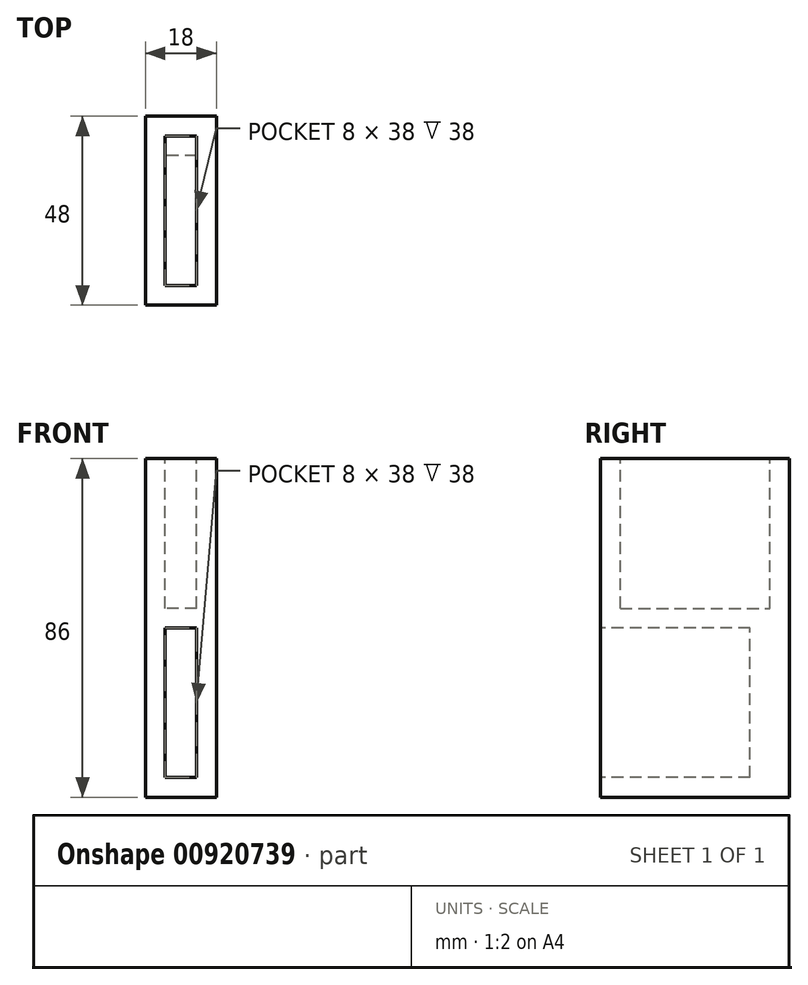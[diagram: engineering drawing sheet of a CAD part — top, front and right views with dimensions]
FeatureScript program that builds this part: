
annotation { "Feature Type Name" : "Feature", "Feature Type Description" : "" }
export const myFeature = defineFeature(function(context is Context, id is Id, definition is map)
    precondition{}
    {
        {
            var Q0;
            Q0=qCreatedBy(makeId("Top.planeOp"),FACE);
            var sketch = newSketch(context, id + "F0", { "sketchPlane" : qUnion([Q0])});
            skLineSegment(sketch, "E0.bottom", {"start": v(0, 0) * mm, "end": v(-18, 0) * mm});
            skLineSegment(sketch, "E0.top", {"start": v(0, -48) * mm, "end": v(-18, -48) * mm});
            skLineSegment(sketch, "E0.left", {"start": v(0, 0) * mm, "end": v(0, -48) * mm});
            skLineSegment(sketch, "E0.right", {"start": v(-18, 0) * mm, "end": v(-18, -48) * mm});
            skSolve(sketch);
        }
        {
            var Q0;
            Q0=makeQuery(id+"F0.imprint","IMPRINT",FACE,{"disambiguationData":[TD([[makeQuery(id+"F0.imprint","IMPRINT",EDGE,{"derivedFrom":sQuery(id+"F0.wireOp",EDGE,"E0.bottom")}),1.0]])]});
            extrude(context, id + "F1", {"entities" : qUnion([Q0]), "depth" : 86 * mm, "offsetDistance" : 25 * mm});
        }
        {
            var Q0;
            Q0=makeQuery(id+"F1.opExtrude","CAP_FACE",FACE,{"disambiguationData":[OSD([sQuery(id+"F0.wireOp",EDGE,"E0.bottom"),sQuery(id+"F0.wireOp",EDGE,"E0.top"),sQuery(id+"F0.wireOp",EDGE,"E0.left"),sQuery(id+"F0.wireOp",EDGE,"E0.right")])],"isStart":false});
            var sketch = newSketch(context, id + "F2", { "sketchPlane" : qUnion([Q0])});
            skLineSegment(sketch, "E1.bottom", {"start": v(-5, -43) * mm, "end": v(-13, -43) * mm});
            skLineSegment(sketch, "E1.top", {"start": v(-5, -5) * mm, "end": v(-13, -5) * mm});
            skLineSegment(sketch, "E1.left", {"start": v(-5, -43) * mm, "end": v(-5, -5) * mm});
            skLineSegment(sketch, "E1.right", {"start": v(-13, -43) * mm, "end": v(-13, -5) * mm});
            skSolve(sketch);
        }
        {
            var Q0;
            Q0=makeQuery(id+"F2.imprint","IMPRINT",FACE,{"disambiguationData":[TD([[makeQuery(id+"F2.imprint","IMPRINT",EDGE,{"derivedFrom":sQuery(id+"F2.wireOp",EDGE,"E1.bottom")}),-1.0]])]});
            extrude(context, id + "F3", {"entities" : qUnion([Q0]), "operationType" : NewBodyOperationType.REMOVE, "oppositeDirection" : true, "depth" : 38 * mm, "offsetDistance" : 25 * mm});
        }
        {
            var Q0;
            Q0=makeQuery(id+"F1.opExtrude","SWEPT_FACE",FACE,{"disambiguationData":[OSD([sQuery(id+"F0.wireOp",EDGE,"E0.top")])]});
            var sketch = newSketch(context, id + "F4", { "sketchPlane" : qUnion([Q0])});
            skLineSegment(sketch, "E2.bottom", {"start": v(-5, 5) * mm, "end": v(-13, 5) * mm});
            skLineSegment(sketch, "E2.top", {"start": v(-5, 43) * mm, "end": v(-13, 43) * mm});
            skLineSegment(sketch, "E2.left", {"start": v(-5, 5) * mm, "end": v(-5, 43) * mm});
            skLineSegment(sketch, "E2.right", {"start": v(-13, 5) * mm, "end": v(-13, 43) * mm});
            skSolve(sketch);
        }
        {
            var Q0;
            Q0=makeQuery(id+"F4.imprint","IMPRINT",FACE,{"disambiguationData":[TD([[makeQuery(id+"F4.imprint","IMPRINT",EDGE,{"derivedFrom":sQuery(id+"F4.wireOp",EDGE,"E2.bottom")}),-1.0]])]});
            extrude(context, id + "F5", {"entities" : qUnion([Q0]), "operationType" : NewBodyOperationType.REMOVE, "oppositeDirection" : true, "depth" : 38 * mm, "offsetDistance" : 25 * mm});
        }
    });
